# Revit family: lzstl8wslp
name_source: partatom
category: Plumbing Fixtures
units: mm (PartAtom-declared; Revit-internal decimal feet)

## family parameters
Always vertical = Yes
Cut with Voids When Loaded = No
OmniClass Number = 23.45.00.00
OmniClass Title = Sanitary, Laundry, and Cleaning Equipment
Part Type = Normal
Room Calculation Point = No
Round Connector Dimension = Use Radius
Shared = No
Work Plane-Based = No

## types (4) — shared parameters
Activation = Push Bars
Basin Material = Metal - Steel - Stainless - Chrome
Bubbler = Flexi-Guard
CW Connection = Yes
Cooler Depth = 1' - 7"
Cooler Rear Panel Depth = 0' - 6 43/256"
Cooler Separation = 0' - 0"
Cooler Width = 1' - 6 57/64"
Description = EZ ADA
Dispenser ADA Height = 2' - 3 1/32"
Dispenser Depth = 0' - 8 25/64"
Filter = EWF 172
Floor to Bottom = 1' - 0 1/2"
Frost Resist = -
Glass Filter = -
HW Connection = No
Louver Screens = -
Lower Cooler Bottom = 1' - 0 1/2"
Lower Cooler Height = 1' - 8 3/8"
Lower Orifice Height = 2' - 8 7/8"
Manufacturer = Elkay
Orifice to Rim = 0' - 1 9/16"
Other Features = -
Panel Material = Metal - Steel - Stainless - Color 3
Refrigerated = Yes
Rim to Dispenser = 0' - 4 9/32"
Rim to Top of Bottom Panel = 0' - 5 9/32"
TOP SKETCH = Yes
Top Panel Material = Metal - Steel - Stainless - Color 2
Type = Bi-Level
URL = http://www.elkay.com
Upper Cooler Bottom = 1' - 6"
Upper Cooler Height = 1' - 8 3/8"
Upper Orifice Height = 3' - 2 3/8"
Upper Rim Height = 3' - 0 13/16"
Vent Connection = No
Version = 1.0.0.0
Volts/Hertz = 115V/60Hz
Waste Connection = Yes
Water Service Flow = 0 GPM
Water Service Size Radius = 0' - 0 1/4"

## per-type parameters (varying)
| type | Model |
| LZSTL8WSLP - LHHS | LZSTL8WSLP - LHHS |
| LZSTL8WSSP - LHHS | LZSTL8WSSP - LHHS |
| LZSTL8WSLVP - LHHS | LZSTL8WSLVP - LHHS |
| LZSTL8WSSVP-LHHS | LZSTL8WSSVP - LHHS |

## geometry (parser evidence)
native form markers: Extrusion x3, Sweep x40
no freeform markers — native parametric forms only
